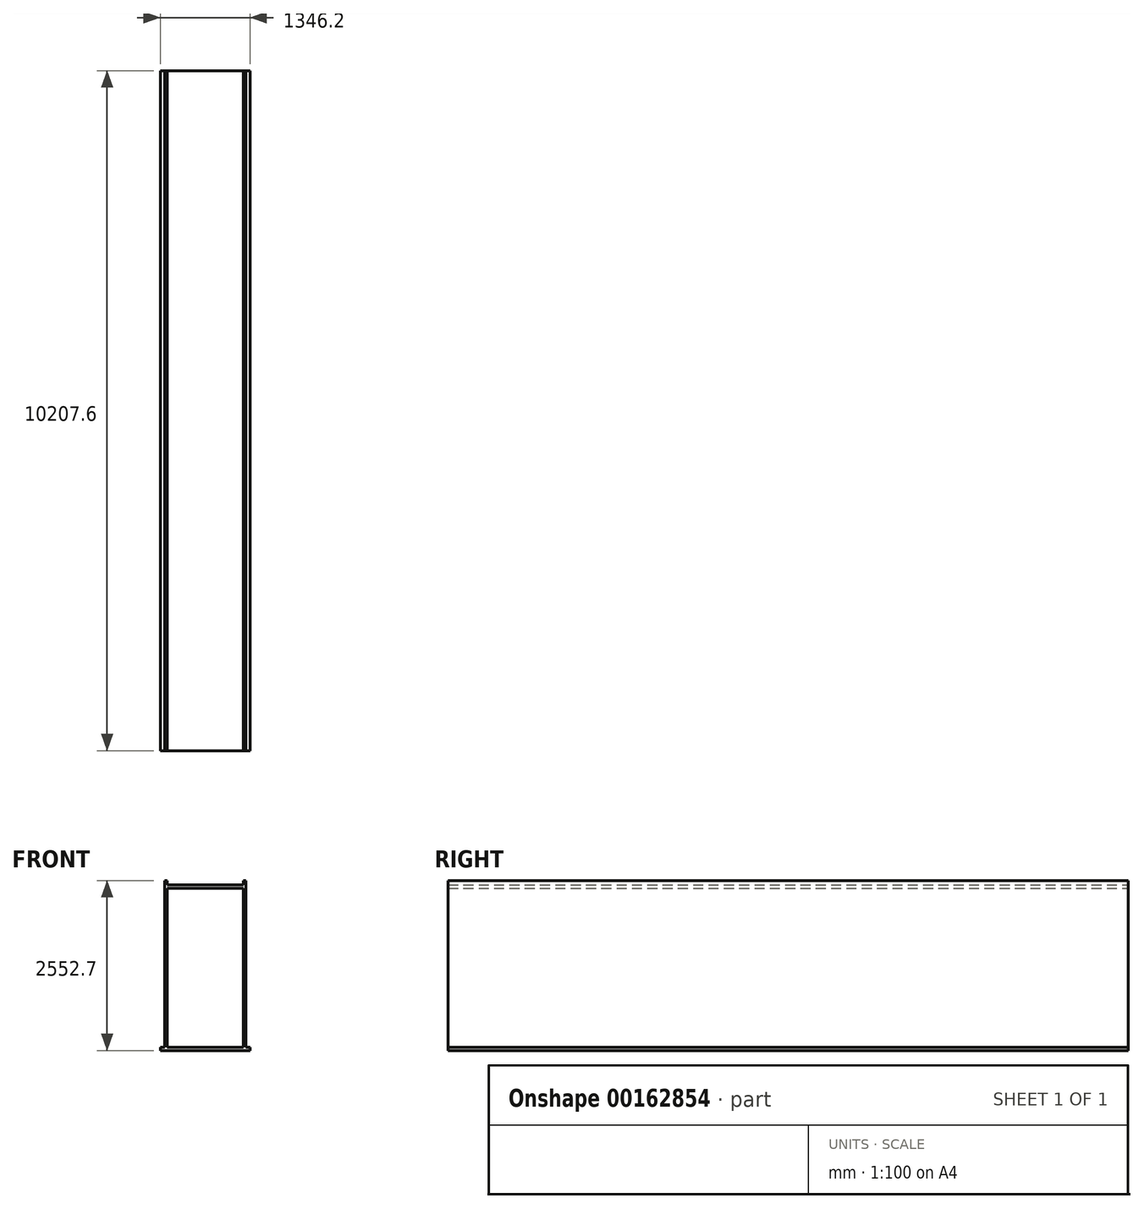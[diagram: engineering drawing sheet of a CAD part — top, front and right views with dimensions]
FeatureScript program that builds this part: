
annotation { "Feature Type Name" : "Feature", "Feature Type Description" : "" }
export const myFeature = defineFeature(function(context is Context, id is Id, definition is map)
    precondition{}
    {
        {
            var Q0;
            Q0=qCreatedBy(makeId("Front.planeOp"),FACE);
            var sketch = newSketch(context, id + "F0", { "sketchPlane" : qUnion([Q0])});
            skLineSegment(sketch, "E0.bottom", {"start": v(673.1, -25.4) * mm, "end": v(-673.1, -25.4) * mm});
            skLineSegment(sketch, "E0.top", {"start": v(673.1, 25.4) * mm, "end": v(-673.1, 25.4) * mm});
            skLineSegment(sketch, "E0.left", {"start": v(673.1, -25.4) * mm, "end": v(673.1, 25.4) * mm});
            skLineSegment(sketch, "E0.right", {"start": v(-673.1, -25.4) * mm, "end": v(-673.1, 25.4) * mm});
            skPoint(sketch, "E0.middle", {"position": v(0, 0) * mm});
            skLineSegment(sketch, "E1.bottom", {"start": v(-571.5, 25.4) * mm, "end": v(-609.6, 25.4) * mm});
            skLineSegment(sketch, "E1.top", {"start": v(-571.5, 2527.3) * mm, "end": v(-609.6, 2527.3) * mm});
            skLineSegment(sketch, "E1.left", {"start": v(-571.5, 25.4) * mm, "end": v(-571.5, 2527.3) * mm});
            skLineSegment(sketch, "E1.right", {"start": v(-609.6, 25.4) * mm, "end": v(-609.6, 2527.3) * mm});
            skLineSegment(sketch, "E2.MirrorCS", {"start": v(571.5, 2527.3) * mm, "end": v(609.6, 2527.3) * mm});
            skLineSegment(sketch, "E3.MirrorCS", {"start": v(609.6, 25.4) * mm, "end": v(609.6, 2527.3) * mm});
            skLineSegment(sketch, "E4.MirrorCS", {"start": v(571.5, 25.4) * mm, "end": v(571.5, 2527.3) * mm});
            skLineSegment(sketch, "E5.bottom", {"start": v(-571.5, 2463.8) * mm, "end": v(571.5, 2463.8) * mm});
            skLineSegment(sketch, "E5.top", {"start": v(-571.5, 2413) * mm, "end": v(571.5, 2413) * mm});
            skLineSegment(sketch, "E5.left", {"start": v(-571.5, 2463.8) * mm, "end": v(-571.5, 2413) * mm});
            skLineSegment(sketch, "E5.right", {"start": v(571.5, 2463.8) * mm, "end": v(571.5, 2413) * mm});
            skSolve(sketch);
        }
        {
            var Q0;
            Q0 = qSketchRegion(id + "F0", true);
            extrude(context, id + "F1", {"entities" : qUnion([Q0]), "depth" : 10207.62 * mm});
        }
    });
